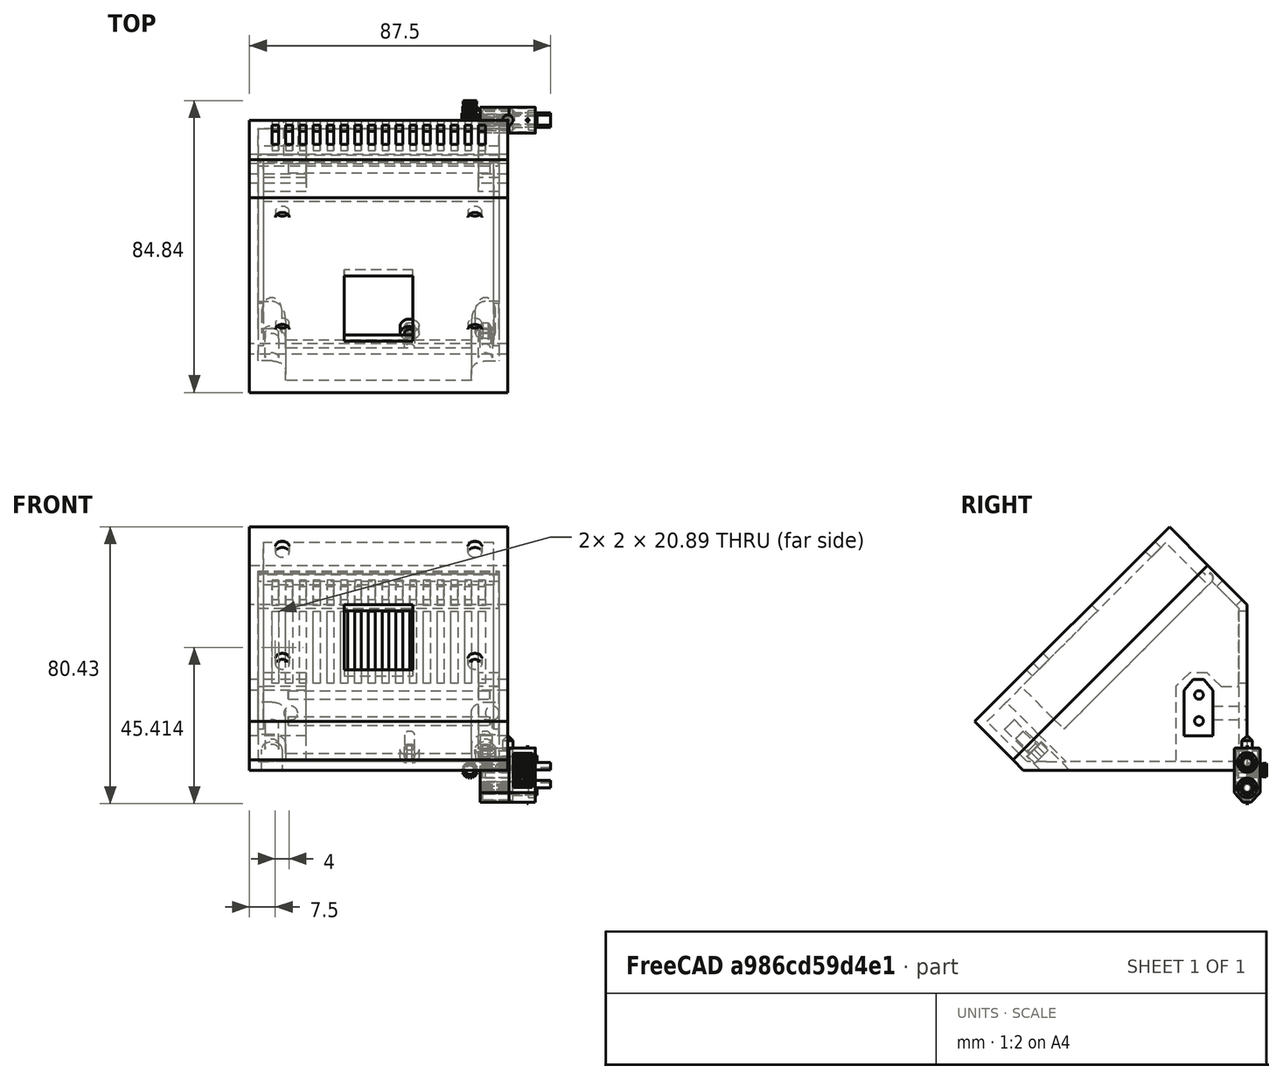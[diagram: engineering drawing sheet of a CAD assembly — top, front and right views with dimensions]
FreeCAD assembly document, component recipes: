
FREECAD ASSEMBLY — COMPONENT RECIPES ("moduleLidl_002_surBase35mm_009.1")

This assembly document has 8 components, labeled P0..P7 below (a component is one placed body or linked part). 4 of them carry a construction recipe — the FreeCAD feature program that regenerates the part from scratch, quoted from this document or its linked companion documents; the rest are supplied as boundary geometry only. No exploded tour is included for this assembly.
COMPONENT P0 — geometry summary ("adapt"; no construction recipe available for this part):
  bounding box: 65.0 x 49.5 x 49.5 mm
  tessellated surface: 2,488 triangles
  volume: 18576 mm^3 (12% of its bounding box)
COMPONENT P1 — geometry summary ("fuse"; no construction recipe available for this part):
  bounding box: 31.7 x 29.8 x 15.0 mm
  tessellated surface: 6,264 triangles
  volume: 2885 mm^3 (20% of its bounding box)
  symmetry: mirror-symmetric across its x mid-plane
COMPONENT P2 — recipe-attached ("tigeLaiton001", modeled in this document).
Construction recipe (the document's own serialized feature program — sketch geometry with constraints, then the solid features built on it; lengths are millimeters unless a unit is written):

FEATURE [PartDesign::Plane] DatumPlane012  label="planBaseTige"
  AttachmentOffset = pos=(0,0,-5.18) rot=(0,0,1;0rad)
  Length = 60
  MapMode = 5
  Placement = pos=(-5.18,1.2e-15,-1.2e-15) rot=(0.57735,0.57735,0.57735;2.0944rad)
  ResizeMode = 0
  Support = -> [YZ_Plane012]
  Width = 60
  expr: .AttachmentOffset.Base.z = -<<tige>>.planBaseTigeposX
FEATURE [Sketcher::SketchObject] Sketch032  label="sk_tiges"
  FullyConstrained = true
  MapMode = 5
  Placement = pos=(-5.18,1.2e-15,-1.2e-15) rot=(0.57735,0.57735,0.57735;2.0944rad)
  Support = -> [DatumPlane012]
  expr: Constraints[0] = <<tige>>.tigeDiam
  expr: Constraints[1] = <<tige>>.tigePosY
  expr: Constraints[2] = <<tige>>.tigePosX
  sketch-geometry (1):
    g0: Circle CenterX=-14 CenterY=14.3 CenterZ=0 NormalX=0 NormalY=0 NormalZ=1 AngleXU=0 Radius=1.25
  constraints (3):
    c: Diameter(g0) = 2.5
    c: DistanceY(g-1,g0) = 14.3
    c: DistanceX(g0,g-1) = 14
FEATURE [PartDesign::Pad] Pad017  label="tigeBasse"
  AllowMultiFace = false
  Direction = (1,-1e-16,1e-16)
  Length = 58.62
  Length2 = 100
  Placement = pos=(-5.18,1e-15,-1e-15) rot=(0.57735,0.57735,0.57735;2.0944rad)
  Profile = -> Sketch032
  Reversed = true
  Type = 0
  expr: Length = <<tige>>.tigeLong
FEATURE [PartDesign::Body] Body007  label="tigeLaiton"
  Group = -> [DatumPlane012,Sketch032,Pad017]
  Origin = -> Origin016
  Tip = -> Pad017
FEATURE [PartDesign::Plane] DatumPlane013  label="planTige2"
  AttachmentOffset = pos=(0,0,-5.18) rot=(0,0,1;0rad)
  Length = 60
  MapMode = 5
  Placement = pos=(-5.18,1.2e-15,-1.2e-15) rot=(0.57735,0.57735,0.57735;2.0944rad)
  ResizeMode = 0
  Support = -> [YZ_Plane014]
  Width = 60
  expr: .AttachmentOffset.Base.z = -<<tige>>.planBaseTigeposX
FEATURE [Sketcher::SketchObject] Sketch033  label="sk_tige2"
  FullyConstrained = true
  MapMode = 5
  Placement = pos=(-5.18,1.2e-15,-1.2e-15) rot=(0.57735,0.57735,0.57735;2.0944rad)
  Support = -> [DatumPlane013]
  expr: Constraints[0] = <<tige>>.tigeDiam
  expr: Constraints[1] = <<tige>>.tigePosX
  expr: Constraints[2] = <<tige>>.tigePosY + <<tige>>.xtEcartBroches
  sketch-geometry (1):
    g0: Circle CenterX=-14 CenterY=21.86 CenterZ=0 NormalX=0 NormalY=0 NormalZ=1 AngleXU=0 Radius=1.25
  constraints (3):
    c: Diameter(g0) = 2.5
    c: DistanceX(g0,g-1) = 14
    c: DistanceY(g-1,g0) = 21.86
FEATURE [PartDesign::Pad] Pad018
  AllowMultiFace = false
  Direction = (1,-1e-16,1e-16)
  Length = 58.62
  Length2 = 100
  Placement = pos=(-5.18,1e-15,-1e-15) rot=(0.57735,0.57735,0.57735;2.0944rad)
  Profile = -> Sketch033
  Reversed = true
  Type = 0
  expr: Length = <<tige>>.tigeLong
FEATURE [PartDesign::Body] Body008  label="tige2"
  Group = -> [DatumPlane013,Sketch033,Pad018]
  Origin = -> Origin018
  Tip = -> Pad018
COMPONENT P3 — geometry summary ("xtVisInsertFix"; no construction recipe available for this part):
  bounding box: 20.2 x 17.7 x 16.6 mm
  tessellated surface: 21,322 triangles
  volume: 1306 mm^3 (22% of its bounding box)
COMPONENT P4 — recipe-attached ("visInsertFavFix", modeled in this document).
Construction recipe (the document's own serialized feature program — sketch geometry with constraints, then the solid features built on it; lengths are millimeters unless a unit is written):

FEATURE [Sketcher::SketchObject] Sketch034  label="Sketch"
  FullyConstrained = false
  MapMode = 5
  Support = -> [XY_Plane015]
  sketch-geometry (1):
    g0: Circle CenterX=0 CenterY=0 CenterZ=0 NormalX=0 NormalY=0 NormalZ=1 AngleXU=0 Radius=2.75
  constraints (2):
    c: Coincident(g0,g-1)
    c: Diameter(g0) = 5.5
FEATURE [PartDesign::Pad] Pad019  label="tete"
  AllowMultiFace = false
  Direction = (1,1,1)
  Length = 3
  Length2 = 100
  Profile = -> Sketch034
  Type = 0
FEATURE [Sketcher::SketchObject] Sketch001
  FullyConstrained = false
  MapMode = 5
  Placement = pos=(0,0,0) rot=(1,0,0;3.14159rad)
  Support = -> [Pad019]
  sketch-geometry (1):
    g0: Circle CenterX=0 CenterY=0 CenterZ=0 NormalX=0 NormalY=0 NormalZ=1 AngleXU=0 Radius=1.5
  constraints (2):
    c: Coincident(g0,g-1)
    c: Diameter(g0) = 3
FEATURE [PartDesign::Pad] Pad020  label="corps"
  AllowMultiFace = false
  BaseFeature = -> Pad019
  Direction = (1,1,1)
  Length = 6
  Length2 = 100
  Profile = -> Sketch001
  Type = 0
FEATURE [PartDesign::Plane] DatumPlane014
  AttachmentOffset = pos=(0,0,3) rot=(0,0,1;0rad)
  Length = 60
  MapMode = 5
  Placement = pos=(0,0,3) rot=(0,0,1;0rad)
  ResizeMode = 0
  Support = -> [XY_Plane015]
  Width = 60
FEATURE [Sketcher::SketchObject] Sketch035  label="Sketch002"
  FullyConstrained = false
  MapMode = 5
  Placement = pos=(0,0,3) rot=(0,0,1;0rad)
  Support = -> [DatumPlane014]
  sketch-geometry (7):
    g0: LineSegment StartX=0.721688 StartY=-1.25 StartZ=0 EndX=1.44338 EndY=1.0119e-12 EndZ=0
    g1: LineSegment StartX=1.44338 StartY=1.0119e-12 StartZ=0 EndX=0.721688 EndY=1.25 EndZ=0
    g2: LineSegment StartX=0.721688 StartY=1.25 StartZ=0 EndX=-0.721688 EndY=1.25 EndZ=0
    g3: LineSegment StartX=-0.721688 StartY=1.25 StartZ=0 EndX=-1.44338 EndY=8.689e-13 EndZ=0
    g4: LineSegment StartX=-1.44338 StartY=8.689e-13 StartZ=0 EndX=-0.721688 EndY=-1.25 EndZ=0
    g5: LineSegment StartX=-0.721688 StartY=-1.25 StartZ=0 EndX=0.721688 EndY=-1.25 EndZ=0
    g6: Circle CenterX=0 CenterY=0 CenterZ=0 NormalX=0 NormalY=0 NormalZ=1 AngleXU=0 Radius=1.44338
  constraints (16):
    c: Coincident(g0,g1)
    c: Coincident(g1,g2)
    c: Coincident(g2,g3)
    c: Coincident(g3,g4)
    c: Coincident(g4,g5)
    c: Coincident(g5,g0)
    c: Equal(g0, g1-g5) x5
    c: PointOnObject(g0,g6)
    c: PointOnObject(g1,g6)
    c: PointOnObject(g2,g6)
    c: PointOnObject(g3,g6)
    c: PointOnObject(g4,g6)
    c: PointOnObject(g5,g6)
    c: Coincident(g6,g-1)
    c: Horizontal(g2)
    c: DistanceY(g0,g1) = 2.5
FEATURE [PartDesign::Pocket] Pocket016  label="emprunte"
  AllowMultiFace = false
  BaseFeature = -> Pad020
  Direction = (1,1,1)
  Length = 4
  Length2 = 100
  Profile = -> Sketch035
  Type = 0
FEATURE [PartDesign::Body] Body009  label="visTHCM3x6_FAV001"
  Group = -> [Sketch034,Pad019,Sketch001,Pad020,DatumPlane014,Sketch035,Pocket016]
  Origin = -> Origin019
  Placement = pos=(-6.5,-61.8718,6.01041) rot=(1,0,0;3.92699rad)
  Tip = -> Pocket016
COMPONENT P5 — recipe-attached ("visInserFavMob", modeled in this document).
Construction recipe (the document's own serialized feature program — sketch geometry with constraints, then the solid features built on it; lengths are millimeters unless a unit is written):

FEATURE [Sketcher::SketchObject] Sketch036
  FullyConstrained = false
  MapMode = 5
  Support = -> [XY_Plane016]
  sketch-geometry (1):
    g0: Circle CenterX=0 CenterY=0 CenterZ=0 NormalX=0 NormalY=0 NormalZ=1 AngleXU=0 Radius=2.75
  constraints (2):
    c: Coincident(g0,g-1)
    c: Diameter(g0) = 5.5
FEATURE [PartDesign::Pad] Pad021  label="tete001"
  AllowMultiFace = false
  Direction = (1,1,1)
  Length = 3
  Length2 = 100
  Profile = -> Sketch036
  Type = 0
FEATURE [Sketcher::SketchObject] Sketch037
  FullyConstrained = false
  MapMode = 5
  Placement = pos=(0,0,0) rot=(1,0,0;3.14159rad)
  Support = -> [Pad021]
  sketch-geometry (1):
    g0: Circle CenterX=0 CenterY=0 CenterZ=0 NormalX=0 NormalY=0 NormalZ=1 AngleXU=0 Radius=1.5
  constraints (2):
    c: Coincident(g0,g-1)
    c: Diameter(g0) = 3
FEATURE [PartDesign::Pad] Pad022  label="corps001"
  AllowMultiFace = false
  BaseFeature = -> Pad021
  Direction = (1,1,1)
  Length = 6
  Length2 = 100
  Profile = -> Sketch037
  Type = 0
FEATURE [PartDesign::Plane] DatumPlane015
  AttachmentOffset = pos=(0,0,3) rot=(0,0,1;0rad)
  Length = 60
  MapMode = 5
  Placement = pos=(0,0,3) rot=(0,0,1;0rad)
  ResizeMode = 0
  Support = -> [XY_Plane016]
  Width = 60
FEATURE [Sketcher::SketchObject] Sketch038
  FullyConstrained = false
  MapMode = 5
  Placement = pos=(0,0,3) rot=(0,0,1;0rad)
  Support = -> [DatumPlane015]
  sketch-geometry (7):
    g0: LineSegment StartX=0.721688 StartY=-1.25 StartZ=0 EndX=1.44338 EndY=1.0119e-12 EndZ=0
    g1: LineSegment StartX=1.44338 StartY=1.0119e-12 StartZ=0 EndX=0.721688 EndY=1.25 EndZ=0
    g2: LineSegment StartX=0.721688 StartY=1.25 StartZ=0 EndX=-0.721688 EndY=1.25 EndZ=0
    g3: LineSegment StartX=-0.721688 StartY=1.25 StartZ=0 EndX=-1.44338 EndY=8.689e-13 EndZ=0
    g4: LineSegment StartX=-1.44338 StartY=8.689e-13 StartZ=0 EndX=-0.721688 EndY=-1.25 EndZ=0
    g5: LineSegment StartX=-0.721688 StartY=-1.25 StartZ=0 EndX=0.721688 EndY=-1.25 EndZ=0
    g6: Circle CenterX=0 CenterY=0 CenterZ=0 NormalX=0 NormalY=0 NormalZ=1 AngleXU=0 Radius=1.44338
  constraints (16):
    c: Coincident(g0,g1)
    c: Coincident(g1,g2)
    c: Coincident(g2,g3)
    c: Coincident(g3,g4)
    c: Coincident(g4,g5)
    c: Coincident(g5,g0)
    c: Equal(g0, g1-g5) x5
    c: PointOnObject(g0,g6)
    c: PointOnObject(g1,g6)
    c: PointOnObject(g2,g6)
    c: PointOnObject(g3,g6)
    c: PointOnObject(g4,g6)
    c: PointOnObject(g5,g6)
    c: Coincident(g6,g-1)
    c: Horizontal(g2)
    c: DistanceY(g0,g1) = 2.5
FEATURE [PartDesign::Pocket] Pocket017  label="emprunte001"
  AllowMultiFace = false
  BaseFeature = -> Pad022
  Direction = (1,1,1)
  Length = 4
  Length2 = 100
  Profile = -> Sketch038
  Type = 0
FEATURE [PartDesign::Body] Body010  label="visTHCM3x6_FAV002"
  Group = -> [Sketch036,Pad021,Sketch037,Pad022,DatumPlane015,Sketch038,Pocket017]
  Origin = -> Origin020
  Placement = pos=(-28.5,-61.8718,6.01041) rot=(1,0,0;3.92699rad)
  Tip = -> Pocket017
COMPONENT P6 — recipe-attached ("BaseModule", modeled in this document).
Construction recipe (the document's own serialized feature program — sketch geometry with constraints, then the solid features built on it; lengths are millimeters unless a unit is written):

FEATURE [PartDesign::FeatureBase] Clone
  BaseFeature = -> Slice_child0
FEATURE [PartDesign::FeatureBase] Clone001
  BaseFeature = -> Slice_child1
FEATURE [PartDesign::Thickness] Thickness
  Base = -> Clone [Face7]
  BaseFeature = -> Clone
  Intersection = false
  Join = 0
  Mode = 0
  Reversed = true
  SupportTransform = false
  Value = 2.5
  expr: Value = <<sp>>.epaisseurParois
FEATURE [PartDesign::Thickness] Thickness001
  Base = -> Clone001 [Face5]
  BaseFeature = -> Clone001
  Intersection = false
  Join = 0
  Mode = 0
  Reversed = true
  SupportTransform = false
  Value = 2.5
  expr: Value = <<sp>>.epaisseurParois
FEATURE [PartDesign::Plane] DatumPlane001  label="planXt"
  AttachmentOffset = pos=(0,0,-2.5) rot=(0,0,1;0rad)
  Length = 110.737
  MapMode = 5
  Placement = pos=(-2.5,6e-16,-6e-16) rot=(0.57735,0.57735,0.57735;2.0944rad)
  ResizeMode = 0
  Support = -> [YZ_Plane002]
  Width = 102.305
  expr: .AttachmentOffset.Base.z = -<<sp>>.epaisseurParois
FEATURE [Sketcher::SketchObject] Sketch002  label="sk_renfortXt"
  FullyConstrained = true
  MapMode = 5
  Placement = pos=(-2.5,6e-16,-6e-16) rot=(0.57735,0.57735,0.57735;2.0944rad)
  Support = -> [DatumPlane001]
  expr: .Constraints.dist = <<sp>>.xt60distanceAngleBord
  expr: .Constraints.epRf = <<sp>>.xt60epRenfort
  expr: Constraints[13] = <<sp>>.xt60largeurFetiere
  expr: Constraints[14] = <<sp>>.xt60hauteur
  expr: Constraints[15] = <<sp>>.xt60hauteurToit
  expr: Constraints[16] = <<sp>>.xt60base
  expr: Constraints[18] = .Constraints.dist
  expr: Constraints[31] = <<sp>>.epaisseurParois
  expr: Constraints[32] = .Constraints.epRf
  expr: Constraints[34] = .Constraints.epRf
  expr: Constraints[45] = <<sp>>.epaisseurParois
  sketch-geometry (17):
    g0: LineSegment StartX=-18.3 StartY=10 StartZ=0 EndX=-18.3 EndY=23.25 EndZ=0
    g1: LineSegment StartX=-18.3 StartY=23.25 StartZ=0 EndX=-15.65 EndY=25.75 EndZ=0
    g2: LineSegment StartX=-15.65 StartY=25.75 StartZ=0 EndX=-12.65 EndY=25.75 EndZ=0
    g3: LineSegment StartX=-12.65 StartY=25.75 StartZ=0 EndX=-10 EndY=23.25 EndZ=0
    g4: LineSegment StartX=-10 StartY=23.25 StartZ=0 EndX=-10 EndY=10 EndZ=0
    g5: LineSegment StartX=-10 StartY=10 StartZ=0 EndX=-18.3 EndY=10 EndZ=0
    g6: LineSegment StartX=-14.15 StartY=10 StartZ=0 EndX=-14.15 EndY=25.75 EndZ=0
    g7: LineSegment StartX=-16.6431 StartY=28.25 StartZ=0 EndX=-20.8 EndY=24.3284 EndZ=0
    g8: LineSegment StartX=-20.8 StartY=24.3284 StartZ=0 EndX=-20.8 EndY=2.5 EndZ=0
    g9: LineSegment StartX=-20.8 StartY=2.5 StartZ=0 EndX=-7.5 EndY=2.5 EndZ=0
    g10: LineSegment StartX=-7.5 StartY=2.5 StartZ=0 EndX=-7.5 EndY=24.3284 EndZ=0
    g11: LineSegment StartX=-7.5 StartY=24.3284 StartZ=0 EndX=-11.6569 EndY=28.25 EndZ=0
    g12: LineSegment StartX=-11.6569 StartY=28.25 StartZ=0 EndX=-16.6431 EndY=28.25 EndZ=0
    g13: LineSegment StartX=-7.5 StartY=24.3284 StartZ=0 EndX=-2.5 EndY=24.3284 EndZ=0
    g14: LineSegment StartX=-2.5 StartY=24.3284 StartZ=0 EndX=-2.5 EndY=2.5 EndZ=0
    g15: LineSegment StartX=-2.5 StartY=2.5 StartZ=0 EndX=-7.5 EndY=2.5 EndZ=0
    g16: LineSegment StartX=-7.5 StartY=2.5 StartZ=0 EndX=-7.5 EndY=24.3284 EndZ=0
  constraints (46):
    c: Vertical(g0)
    c: Coincident(g0,g1)
    c: Coincident(g1,g2)
    c: Horizontal(g2)
    c: Coincident(g2,g3)
    c: Coincident(g3,g4)
    c: Vertical(g4)
    c: Coincident(g4,g5)
    c: Coincident(g5,g0)
    c: Horizontal(g5)
    c: Symmetric(g1,g2,g6)
    c: Equal(g0,g4)
    c: Symmetric(g0,g4,g6)
    c: DistanceX(g2,g2) = 3
    c: DistanceY(g4,g4) = 13.25
    c: DistanceY(g3,g2) = 2.5
    c: DistanceX(g5,g5) = 8.3
    c: DistanceX(g4,g-1) = 10  'dist'
    c: DistanceY(g-1,g4) = 10
    c: Coincident(g7,g8)
    c: Vertical(g8)
    c: Coincident(g8,g9)
    c: Horizontal(g9)
    c: Coincident(g9,g10)
    c: Coincident(g10,g11)
    c: Coincident(g11,g12)
    c: Coincident(g12,g7)
    c: Symmetric(g7,g10,g6)
    c: Symmetric(g7,g11,g6)
    c: Symmetric(g8,g9,g6)
    c: DistanceX(g8,g0) = 2.5  'epRf'
    c: DistanceY(g-1,g9) = 2.5
    c: Distance(g7,g1) = 2.5
    c: Parallel(g1,g7)
    c: DistanceY(g2,g11) = 2.5
    c: Coincident(g13,g14)
    c: Coincident(g14,g15)
    c: Coincident(g15,g16)
    c: Coincident(g16,g13)
    c: Horizontal(g13)
    c: Horizontal(g15)
    c: Vertical(g14)
    c: Vertical(g16)
    c: Coincident(g13,g11)
    c: Horizontal(g14,g9)
    c: DistanceX(g14,g-1) = 2.5
FEATURE [PartDesign::Pad] Pad001  label="renfortXt"
  AllowMultiFace = false
  BaseFeature = -> Thickness
  Direction = (1,-1e-16,1e-16)
  Length = 70
  Length2 = 100
  Profile = -> Sketch002
  Reversed = true
  Type = 0
  expr: Length = <<sp>>.largeurModuleBase - 2 * <<sp>>.epaisseurParois
FEATURE [Sketcher::SketchObject] Sketch003  label="sk_trouXt"
  FullyConstrained = true
  MapMode = 5
  Placement = pos=(0,0,0) rot=(0.57735,0.57735,0.57735;2.0944rad)
  Support = -> [YZ_Plane002]
  expr: .Constraints.dist = <<sp>>.xt60distanceAngleBord
  expr: Constraints[13] = <<sp>>.xt60base
  expr: Constraints[14] = <<sp>>.xt60hauteur
  expr: Constraints[15] = <<sp>>.xt60hauteurToit + <<sp>>.xtJeu
  expr: Constraints[16] = <<sp>>.xt60largeurFetiere
  expr: Constraints[18] = .Constraints.dist
  sketch-geometry (7):
    g0: LineSegment StartX=-18.3 StartY=10 StartZ=0 EndX=-18.3 EndY=23.25 EndZ=0
    g1: LineSegment StartX=-18.3 StartY=23.25 StartZ=0 EndX=-15.65 EndY=26.35 EndZ=0
    g2: LineSegment StartX=-15.65 StartY=26.35 StartZ=0 EndX=-12.65 EndY=26.35 EndZ=0
    g3: LineSegment StartX=-12.65 StartY=26.35 StartZ=0 EndX=-10 EndY=23.25 EndZ=0
    g4: LineSegment StartX=-10 StartY=23.25 StartZ=0 EndX=-10 EndY=10 EndZ=0
    g5: LineSegment StartX=-10 StartY=10 StartZ=0 EndX=-18.3 EndY=10 EndZ=0
    g6: LineSegment StartX=-14.15 StartY=10 StartZ=0 EndX=-14.15 EndY=26.35 EndZ=0
  constraints (19):
    c: Vertical(g0)
    c: Coincident(g0,g1)
    c: Coincident(g1,g2)
    c: Horizontal(g2)
    c: Coincident(g2,g3)
    c: Coincident(g3,g4)
    c: Coincident(g4,g5)
    c: Coincident(g5,g0)
    c: Horizontal(g5)
    c: Symmetric(g1,g2,g6)
    c: Symmetric(g0,g3,g6)
    c: Vertical(g6)
    c: Symmetric(g0,g4,g6)
    c: DistanceX(g5,g5) = 8.3
    c: DistanceY(g4,g4) = 13.25
    c: DistanceY(g3,g2) = 3.1
    c: DistanceX(g2,g2) = 3
    c: DistanceX(g4,g-1) = 10  'dist'
    c: DistanceY(g-1,g4) = 10
FEATURE [PartDesign::Pocket] Pocket
  AllowMultiFace = false
  BaseFeature = -> Pad001
  Direction = (-1,2e-16,-3e-16)
  Length = 75
  Length2 = 100
  Profile = -> Sketch003
  Type = 0
  expr: Length = <<sp>>.largeurModuleBase
FEATURE [PartDesign::Plane] DatumPlane002  label="planDecoupeRenfortXt"
  AttachmentOffset = pos=(0,0,2.5) rot=(0,0,1;0rad)
  Length = 118.392
  MapMode = 5
  Placement = pos=(0,-2.5,-6e-16) rot=(1,0,0;1.5708rad)
  ResizeMode = 0
  Support = -> [XZ_Plane002]
  Width = 102.961
  expr: .AttachmentOffset.Base.z = <<sp>>.epaisseurParois
FEATURE [Sketcher::SketchObject] Sketch004  label="sk_decoupRenfXt"
  FullyConstrained = true
  MapMode = 5
  Placement = pos=(0,-2.5,-6e-16) rot=(1,0,0;1.5708rad)
  Support = -> [DatumPlane002]
  expr: Constraints[10] = <<sp>>.xt60LongueurRenfortPetit + <<sp>>.epaisseurParois
  expr: Constraints[11] = <<sp>>.largeurModuleBase - (<<sp>>.xt60longueurRenfortGrand + <<sp>>.epaisseurParois)
  expr: Constraints[8] = <<sp>>.epaisseurParois
  expr: Constraints[9] = <<sp>>.xt60distanceAngleBord + <<sp>>.xt60hauteur + <<sp>>.xt60hauteurToit + <<sp>>.xt60epRenfort
  sketch-geometry (4):
    g0: LineSegment StartX=-58.5 StartY=28.25 StartZ=0 EndX=-8.5 EndY=28.25 EndZ=0
    g1: LineSegment StartX=-8.5 StartY=28.25 StartZ=0 EndX=-8.5 EndY=2.5 EndZ=0
    g2: LineSegment StartX=-8.5 StartY=2.5 StartZ=0 EndX=-58.5 EndY=2.5 EndZ=0
    g3: LineSegment StartX=-58.5 StartY=2.5 StartZ=0 EndX=-58.5 EndY=28.25 EndZ=0
  constraints (12):
    c: Coincident(g0,g1)
    c: Coincident(g1,g2)
    c: Coincident(g2,g3)
    c: Coincident(g3,g0)
    c: Horizontal(g0)
    c: Horizontal(g2)
    c: Vertical(g1)
    c: Vertical(g3)
    c: DistanceY(g-1,g1) = 2.5
    c: DistanceY(g-1,g0) = 28.25
    c: DistanceX(g1,g-1) = 8.5
    c: DistanceX(g2,g-1) = 58.5
FEATURE [PartDesign::Pocket] Pocket001  label="decoupeRenfXt"
  AllowMultiFace = false
  BaseFeature = -> Pocket
  Direction = (0,1,2e-16)
  Length = 23.3
  Length2 = 100
  Profile = -> Sketch004
  Reversed = true
  Type = 0
  expr: Length = <<sp>>.xt60distanceAngleBord + <<sp>>.xt60base + 2 * <<sp>>.xt60epRenfort
FEATURE [Sketcher::SketchObject] Sketch005  label="xt60PercagePostMale"
  FullyConstrained = true
  MapMode = 5
  Placement = pos=(0,0,0) rot=(1,0,0;1.5708rad)
  Support = -> [XZ_Plane002]
  expr: Constraints[0] = <<sp>>.insertDiamPercage
  expr: Constraints[1] = <<sp>>.insertDistanceTrouBordMale
  expr: Constraints[2] = <<sp>>.insertHauteur
  sketch-geometry (1):
    g0: Circle CenterX=-4.5 CenterY=16.625 CenterZ=0 NormalX=0 NormalY=0 NormalZ=1 AngleXU=0 Radius=2
  constraints (3):
    c: Diameter(g0) = 4
    c: DistanceX(g0,g-1) = 4.5
    c: DistanceY(g-1,g0) = 16.625
FEATURE [PartDesign::Pocket] Pocket002  label="insertXtMale"
  AllowMultiFace = false
  BaseFeature = -> Pocket001
  Direction = (0,1,2e-16)
  Length = 10
  Length2 = 100
  Profile = -> Sketch005
  Reversed = true
  Type = 0
  expr: Length = <<sp>>.insertProfondeurPercage
FEATURE [Sketcher::SketchObject] Sketch006  label="xt60PercagePostFem"
  FullyConstrained = true
  MapMode = 5
  Placement = pos=(0,0,0) rot=(1,0,0;1.5708rad)
  Support = -> [XZ_Plane002]
  expr: Constraints[0] = <<sp>>.insertDiamPercage
  expr: Constraints[1] = <<sp>>.insertDistanceTrouBordFem
  expr: Constraints[2] = <<sp>>.insertHauteur
  sketch-geometry (1):
    g0: Circle CenterX=-63 CenterY=16.625 CenterZ=0 NormalX=0 NormalY=0 NormalZ=1 AngleXU=0 Radius=2
  constraints (3):
    c: Diameter(g0) = 4
    c: DistanceX(g0,g-1) = 63
    c: DistanceY(g-1,g0) = 16.625
FEATURE [PartDesign::Pocket] Pocket003  label="insertXt60Fem"
  AllowMultiFace = false
  BaseFeature = -> Pocket002
  Direction = (0,1,2e-16)
  Length = 10
  Length2 = 100
  Profile = -> Sketch006
  Reversed = true
  Type = 0
  expr: Length = <<sp>>.insertProfondeurPercage
FEATURE [PartDesign::Plane] DatumPlane003
  AttachmentOffset = pos=(0,0,2.5) rot=(0,0,1;0rad)
  Length = 119.287
  MapMode = 2
  Placement = pos=(0,0,2.5) rot=(0,0,1;0rad)
  ResizeMode = 0
  Support = -> [XY_Plane002]
  Width = 112.287
  expr: .AttachmentOffset.Base.z = <<sp>>.epaisseurParois
FEATURE [PartDesign::Plane] DatumPlane004  label="planTrancheur"
  AttachmentOffset = pos=(0,0,71) rot=(-1,0,0;0.785398rad)
  Length = 122.411
  MapMode = 5
  Placement = pos=(0,-71,-1.58e-14) rot=(1,0,0;0.785398rad)
  ResizeMode = 0
  Support = -> [XZ_Plane002]
  Width = 147.971
  expr: .AttachmentOffset.Base.z = <<sp>>.planTrancheur
FEATURE [Sketcher::SketchObject] Sketch008
  FullyConstrained = true
  MapMode = 5
  Placement = pos=(0,-71,-2.13e-14) rot=(1,0,0;0.785398rad)
  Support = -> [DatumPlane004]
  expr: .Constraints.dist = <<sp>>.epaisseurParois
  expr: Constraints[13] = <<sp>>.epaisseurParois
  expr: Constraints[16] = <<sp>>.insertDiamPercage / 2 + <<sp>>.insertFAVMargeDist
  expr: Constraints[1] = <<sp>>.insertFavDistAuZeroDuPLan
  expr: Constraints[21] = <<sp>>.insertFAVDistBord
  expr: Constraints[22] = <<sp>>.largeurModuleBase - <<sp>>.epaisseurParois
  sketch-geometry (7):
    g0: LineSegment StartX=-2.5 StartY=4.24264 StartZ=0 EndX=-72.5 EndY=4.24264 EndZ=0
    g1: LineSegment StartX=-6.5 StartY=14.7426 StartZ=0 EndX=-2.5 EndY=14.7426 EndZ=0
    g2: LineSegment StartX=-2.5 StartY=14.7426 StartZ=0 EndX=-2.5 EndY=6.74264 EndZ=0
    g3: LineSegment StartX=-2.5 StartY=6.74264 StartZ=0 EndX=-10.5 EndY=6.74264 EndZ=0
    g4: LineSegment StartX=-10.5 StartY=6.74264 StartZ=0 EndX=-10.5 EndY=10.7426 EndZ=0
    g5: ArcOfCircle CenterX=-6.5 CenterY=10.7426 CenterZ=0 NormalX=0 NormalY=0 NormalZ=1 AngleXU=0 Radius=4 StartAngle=1.5708 EndAngle=3.14159
    g6: LineSegment StartX=-6.5 StartY=10.7426 StartZ=0 EndX=-6.5 EndY=6.74264 EndZ=0
  constraints (23):
    c: Horizontal(g0)
    c: DistanceY(g-1,g0) = 4.24264
    c: DistanceX(g0,g-1) = 2.5  'dist'
    c: Horizontal(g1)
    c: Coincident(g1,g2)
    c: Vertical(g2)
    c: Coincident(g2,g3)
    c: Horizontal(g3)
    c: Coincident(g3,g4)
    c: Vertical(g4)
    c: Vertical(g2,g0)
    c: Equal(g3,g2)
    c: Equal(g4,g1)
    c: DistanceY(g0,g2) = 2.5
    c: Coincident(g5,g4)
    c: Coincident(g5,g1)
    c: DistanceX(g5,g2) = 4
    c: Coincident(g6,g5)
    c: PointOnObject(g6,g3)
    c: Vertical(g6)
    c: Vertical(g5,g1)
    c: DistanceX(g3,g3) = 8
    c: DistanceX(g0,g-1) = 72.5
FEATURE [PartDesign::Pad] Pad003  label="padTrouFAVDroite"
  AllowMultiFace = false
  BaseFeature = -> Pocket003
  Direction = (0,-0.707107,0.707107)
  Length = 10
  Length2 = 100
  Profile = -> Sketch008
  Reversed = true
  Type = 3
  UpToFace = -> DatumPlane003
FEATURE [Sketcher::SketchObject] Sketch009
  FullyConstrained = true
  MapMode = 5
  Placement = pos=(0,-71,-2.13e-14) rot=(1,0,0;0.785398rad)
  Support = -> [DatumPlane004]
  expr: .Constraints.larg = <<sp>>.insertFAVDistBord
  expr: Constraints[11] = .Constraints.larg / 2
  expr: Constraints[12] = <<sp>>.largeurModuleBase
  expr: Constraints[13] = <<sp>>.insertFavDistAuZeroDuPLan
  expr: Constraints[14] = <<sp>>.epaisseurParois
  expr: Constraints[15] = <<sp>>.epaisseurParois
  expr: Constraints[8] = .Constraints.larg
  sketch-geometry (6):
    g0: LineSegment StartX=-72.5 StartY=6.74264 StartZ=0 EndX=-64.5 EndY=6.74264 EndZ=0
    g1: LineSegment StartX=-64.5 StartY=6.74264 StartZ=0 EndX=-64.5 EndY=10.7426 EndZ=0
    g2: LineSegment StartX=-68.5 StartY=14.7426 StartZ=0 EndX=-72.5 EndY=14.7426 EndZ=0
    g3: LineSegment StartX=-72.5 StartY=14.7426 StartZ=0 EndX=-72.5 EndY=6.74264 EndZ=0
    g4: ArcOfCircle CenterX=-68.5 CenterY=10.7426 CenterZ=0 NormalX=0 NormalY=0 NormalZ=1 AngleXU=0 Radius=4 StartAngle=0 EndAngle=1.5708
    g5: GeomPoint X=-75 Y=4.24264 Z=0
  constraints (16):
    c: Coincident(g0,g1)
    c: Coincident(g2,g3)
    c: Coincident(g3,g0)
    c: Horizontal(g0)
    c: Horizontal(g2)
    c: Vertical(g1)
    c: Vertical(g3)
    c: DistanceX(g0,g0) = 8  'larg'
    c: DistanceY(g3,g3) = 8
    c: Tangent(g2,g4) = -1.5708
    c: Tangent(g1,g4) = -1.5708
    c: DistanceX(g0,g4) = 4
    c: DistanceX(g5,g-1) = 75
    c: DistanceY(g-1,g5) = 4.24264
    c: DistanceX(g5,g0) = 2.5
    c: DistanceY(g5,g0) = 2.5
FEATURE [PartDesign::Pad] Pad004  label="padTrouFavGauche"
  AllowMultiFace = false
  BaseFeature = -> Pad003
  Direction = (0,-0.707107,0.707107)
  Length = 10
  Length2 = 100
  Profile = -> Sketch009
  Type = 3
  UpToFace = -> DatumPlane003 [Plane]
FEATURE [Sketcher::SketchObject] Sketch010
  FullyConstrained = true
  MapMode = 5
  Placement = pos=(0,-71,-2.13e-14) rot=(1,0,0;0.785398rad)
  Support = -> [DatumPlane004]
  expr: Constraints[0] = <<sp>>.insertFAVDistBord / 2 + <<sp>>.epaisseurParois
  expr: Constraints[1] = <<sp>>.insertFavDistAuZeroDuPLan + <<sp>>.epaisseurParois + <<sp>>.insertFAVDistBord / 2
  expr: Constraints[2] = <<sp>>.insertDiamPercage
  sketch-geometry (1):
    g0: Circle CenterX=-6.5 CenterY=10.7426 CenterZ=0 NormalX=0 NormalY=0 NormalZ=1 AngleXU=0 Radius=2
  constraints (3):
    c: DistanceX(g0,g-1) = 6.5
    c: DistanceY(g-1,g0) = 10.7426
    c: Diameter(g0) = 4
FEATURE [PartDesign::Pocket] Pocket004  label="trouDroit"
  AllowMultiFace = false
  BaseFeature = -> Pad004
  Direction = (0,0.707107,-0.707107)
  Length = 5
  Length2 = 100
  Profile = -> Sketch010
  Type = 1
FEATURE [Sketcher::SketchObject] Sketch011
  FullyConstrained = true
  MapMode = 5
  Placement = pos=(0,-71,-2.13e-14) rot=(1,0,0;0.785398rad)
  Support = -> [DatumPlane004]
  expr: Constraints[0] = <<sp>>.insertDiamPercage
  expr: Constraints[1] = <<sp>>.largeurModuleBase - <<sp>>.epaisseurParois - <<sp>>.insertFAVDistBord / 2
  expr: Constraints[2] = <<sp>>.insertFavDistAuZeroDuPLan + <<sp>>.epaisseurParois + <<sp>>.insertFAVDistBord / 2
  sketch-geometry (1):
    g0: Circle CenterX=-68.5 CenterY=10.7426 CenterZ=0 NormalX=0 NormalY=0 NormalZ=1 AngleXU=0 Radius=2
  constraints (3):
    c: Diameter(g0) = 4
    c: DistanceX(g0,g-1) = 68.5
    c: DistanceY(g-1,g0) = 10.7426
FEATURE [PartDesign::Pocket] Pocket005  label="trouGauche"
  AllowMultiFace = false
  BaseFeature = -> Pocket004
  Direction = (0,0.707107,-0.707107)
  Length = 5
  Length2 = 100
  Profile = -> Sketch011
  Type = 1
FEATURE [PartDesign::Plane] DatumPlane005  label="planTeteVisFav"
  AttachmentOffset = pos=(0,0,68) rot=(-1,0,0;0.785398rad)
  Length = 122.411
  MapMode = 5
  Placement = pos=(0,-68,-1.51e-14) rot=(1,0,0;0.785398rad)
  ResizeMode = 0
  Support = -> [XZ_Plane002]
  Width = 147.971
  expr: .AttachmentOffset.Base.z = <<sp>>.planTrancheur - 3
FEATURE [Sketcher::SketchObject] Sketch012
  ExternalGeometry = -> [Pocket005]
  FullyConstrained = true
  MapMode = 5
  Placement = pos=(0,-68,-1.42e-14) rot=(1,0,0;0.785398rad)
  Support = -> [DatumPlane005]
  expr: Constraints[1] = <<sp>>.visM3DiamEncastrement
  sketch-geometry (2):
    g0: Circle CenterX=-6.5 CenterY=8.62132 CenterZ=0 NormalX=0 NormalY=0 NormalZ=1 AngleXU=0 Radius=3
    g1: Circle CenterX=-68.5 CenterY=8.62132 CenterZ=0 NormalX=0 NormalY=0 NormalZ=1 AngleXU=0 Radius=3
  constraints (4):
    c: Equal(g0,g1)
    c: Diameter(g1) = 6
    c: Coincident(g1,g-4)
    c: Coincident(g-3,g0)
FEATURE [PartDesign::Pocket] Pocket006  label="evidementTeteVisFav"
  AllowMultiFace = false
  BaseFeature = -> Pocket005
  Direction = (0,0.707107,-0.707107)
  Length = 20
  Length2 = 100
  Profile = -> Sketch012
  Type = 1
FEATURE [Sketcher::SketchObject] Sketch014
  FullyConstrained = true
  MapMode = 5
  Placement = pos=(0,0,0) rot=(1,0,0;1.5708rad)
  Support = -> [XZ_Plane002]
  expr: Constraints[12] = <<sp>>.xt60distanceAngleBord + <<sp>>.xt60hauteur + <<sp>>.ventilDistBordFente
  expr: Constraints[13] = <<sp>>.ventilLargeurFentes
  expr: Constraints[14] = <<sp>>.ventilEcartfente / 2
  expr: Constraints[15] = <<sp>>.hauteurDuDos - <<sp>>.ventilDistBordFente
  expr: Constraints[2] = <<sp>>.hauteurDuDos
  expr: Constraints[3] = <<sp>>.largeurModuleBase / 2
  sketch-geometry (5):
    g0: LineSegment StartX=-37.5 StartY=0 StartZ=0 EndX=-37.5 EndY=48.1371 EndZ=0
    g1: LineSegment StartX=-40.5 StartY=46.1371 StartZ=0 EndX=-38.5 EndY=46.1371 EndZ=0
    g2: LineSegment StartX=-38.5 StartY=46.1371 StartZ=0 EndX=-38.5 EndY=25.25 EndZ=0
    g3: LineSegment StartX=-38.5 StartY=25.25 StartZ=0 EndX=-40.5 EndY=25.25 EndZ=0
    g4: LineSegment StartX=-40.5 StartY=25.25 StartZ=0 EndX=-40.5 EndY=46.1371 EndZ=0
  constraints (16):
    c: PointOnObject(g0,g-1)
    c: Vertical(g0)
    c: DistanceY(g0,g0) = 48.1371
    c: DistanceX(g0,g-1) = 37.5
    c: Coincident(g1,g2)
    c: Coincident(g2,g3)
    c: Coincident(g3,g4)
    c: Coincident(g4,g1)
    c: Horizontal(g1)
    c: Horizontal(g3)
    c: Vertical(g2)
    c: Vertical(g4)
    c: DistanceY(g-1,g2) = 25.25
    c: DistanceX(g1,g1) = 2
    c: DistanceX(g2,g0) = 1
    c: DistanceY(g-1,g1) = 46.1371
FEATURE [PartDesign::Pocket] Pocket008  label="ventilFente1"
  AllowMultiFace = false
  BaseFeature = -> Pocket006
  Direction = (0,1,2e-16)
  Length = 2.5
  Length2 = 100
  Profile = -> Sketch014
  Reversed = true
  Type = 0
  expr: Length = <<sp>>.epaisseurParois
FEATURE [PartDesign::LinearPattern] LinearPattern  label="ventilDosRepeat1"
  BaseFeature = -> Pocket008
  Direction = -> Sketch014 [H_Axis]
  Length = 28
  Occurrences = 8
  Originals = -> [Pocket008]
  Reversed = true
  expr: Length = <<sp>>.ventilLargeurRepet
  expr: Occurrences = <<sp>>.ventilNbrFents
FEATURE [PartDesign::LinearPattern] LinearPattern001  label="ventilDosRepeat2"
  BaseFeature = -> LinearPattern
  Direction = -> Sketch014 [H_Axis]
  Length = 32
  Occurrences = 9
  Originals = -> [Pocket008]
  expr: Length = <<sp>>.ventilLargeurRepet + <<sp>>.ventilEcartfente + <<sp>>.ventilLargeurFentes
  expr: Occurrences = <<sp>>.ventilNbrFents + 1
FEATURE [PartDesign::Plane] DatumPlane006  label="planVentilSup"
  AttachmentOffset = pos=(0,0,-48.1371) rot=(1,0,0;0.785398rad)
  Length = 122.411
  MapMode = 5
  Placement = pos=(0,48.1371,1.07e-14) rot=(1,0,0;2.35619rad)
  ResizeMode = 0
  Support = -> [XZ_Plane002]
  Width = 147.971
  expr: .AttachmentOffset.Base.z = -<<sp>>.hauteurDuDos
FEATURE [Sketcher::SketchObject] Sketch015
  FullyConstrained = true
  MapMode = 5
  Placement = pos=(0,48.1371,1.07e-14) rot=(1,0,0;2.35619rad)
  Support = -> [DatumPlane006]
  expr: Constraints[10] = <<sp>>.ventilLargeurFentes
  expr: Constraints[11] = (<<sp>>.largeurModuleBase + <<sp>>.ventilEcartfente) / 2
  expr: Constraints[8] = <<sp>>.distanceAuZeroPlanBorArriere + <<sp>>.ventilDistBordFente
  expr: Constraints[9] = <<sp>>.longPetitRetSupSansFav - 2 * <<sp>>.ventilDistBordFente - <<sp>>.favBordureProf
  sketch-geometry (4):
    g0: LineSegment StartX=-38.5 StartY=78.0926 StartZ=0 EndX=-40.5 EndY=78.0926 EndZ=0
    g1: LineSegment StartX=-40.5 StartY=78.0926 StartZ=0 EndX=-40.5 EndY=70.0761 EndZ=0
    g2: LineSegment StartX=-40.5 StartY=70.0761 StartZ=0 EndX=-38.5 EndY=70.0761 EndZ=0
    g3: LineSegment StartX=-38.5 StartY=70.0761 StartZ=0 EndX=-38.5 EndY=78.0926 EndZ=0
  constraints (12):
    c: Coincident(g0,g1)
    c: Coincident(g1,g2)
    c: Coincident(g2,g3)
    c: Coincident(g3,g0)
    c: Horizontal(g0)
    c: Horizontal(g2)
    c: Vertical(g1)
    c: Vertical(g3)
    c: DistanceY(g-1,g2) = 70.0761
    c: DistanceY(g2,g0) = 8.01652
    c: DistanceX(g0,g0) = 2
    c: DistanceX(g2,g-1) = 38.5
FEATURE [PartDesign::Pocket] Pocket009  label="ventilSupFente"
  AllowMultiFace = false
  BaseFeature = -> LinearPattern001
  Direction = (0,0.707107,0.707107)
  Length = 5
  Length2 = 100
  Profile = -> Sketch015
  Reversed = true
  Type = 0
FEATURE [PartDesign::LinearPattern] LinearPattern002  label="ventilSupRepeat1"
  BaseFeature = -> Pocket009
  Direction = -> Sketch015 [H_Axis]
  Length = 28
  Occurrences = 8
  Originals = -> [Pocket009]
  Reversed = true
  expr: Length = <<sp>>.ventilLargeurRepet
  expr: Occurrences = <<sp>>.ventilNbrFents
FEATURE [PartDesign::LinearPattern] LinearPattern003  label="ventilSupRepeat2"
  BaseFeature = -> LinearPattern002
  Direction = -> Sketch015 [H_Axis]
  Length = 32
  Occurrences = 9
  Originals = -> [Pocket009]
  expr: Length = <<sp>>.ventilLargeurRepet + <<sp>>.ventilEcartfente + <<sp>>.ventilLargeurFentes
  expr: Occurrences = <<sp>>.ventilNbrFents + 1
FEATURE [PartDesign::Plane] DatumPlane007  label="planTrancheurBis"
  AttachmentOffset = pos=(0,0,71) rot=(-1,0,0;0.785398rad)
  Length = 123.775
  MapMode = 5
  Placement = pos=(0,-71,-1.58e-14) rot=(1,0,0;0.785398rad)
  ResizeMode = 0
  Support = -> [XZ_Plane003]
  Width = 165.093
  expr: .AttachmentOffset.Base.z = <<sp>>.planTrancheur
FEATURE [Sketcher::SketchObject] Sketch016  label="sk_insertFavDroit"
  FullyConstrained = true
  MapMode = 5
  Placement = pos=(0,-71,-2.13e-14) rot=(1,0,0;0.785398rad)
  Support = -> [DatumPlane007]
  expr: Constraints[11] = <<sp>>.insertFAVDistBord
  expr: Constraints[14] = <<sp>>.insertFAVDistBord / 2
  expr: Constraints[7] = <<sp>>.epaisseurParois
  expr: Constraints[8] = <<sp>>.insertFavDistAuZeroDuPLan + <<sp>>.epaisseurParois
  expr: Constraints[9] = <<sp>>.insertFAVDistBord
  sketch-geometry (5):
    g0: LineSegment StartX=-6.5 StartY=14.7426 StartZ=0 EndX=-2.5 EndY=14.7426 EndZ=0
    g1: LineSegment StartX=-2.5 StartY=14.7426 StartZ=0 EndX=-2.5 EndY=6.74264 EndZ=0
    g2: LineSegment StartX=-2.5 StartY=6.74264 StartZ=0 EndX=-10.5 EndY=6.74264 EndZ=0
    g3: LineSegment StartX=-10.5 StartY=6.74264 StartZ=0 EndX=-10.5 EndY=10.7426 EndZ=0
    g4: ArcOfCircle CenterX=-6.5 CenterY=10.7426 CenterZ=0 NormalX=0 NormalY=0 NormalZ=1 AngleXU=0 Radius=4 StartAngle=1.5708 EndAngle=3.14159
  constraints (15):
    c: Horizontal(g0)
    c: Coincident(g0,g1)
    c: Vertical(g1)
    c: Coincident(g1,g2)
    c: Horizontal(g2)
    c: Coincident(g2,g3)
    c: Vertical(g3)
    c: DistanceX(g1,g-1) = 2.5
    c: DistanceY(g-1,g1) = 6.74264
    c: DistanceY(g1,g1) = 8
    c: Equal(g3,g0)
    c: DistanceX(g2,g2) = 8
    c: Coincident(g4,g0)
    c: Tangent(g4,g3) = 1.5708
    c: DistanceX(g4,g1) = 4
FEATURE [PartDesign::Pad] Pad005  label="padInsertFavDroit"
  AllowMultiFace = false
  BaseFeature = -> Thickness001
  Direction = (0,-0.707107,0.707107)
  Length = 10
  Length2 = 100
  Profile = -> Sketch016
  Type = 2
FEATURE [Sketcher::SketchObject] Sketch017  label="sp_padInserFavGauch"
  FullyConstrained = true
  MapMode = 5
  Placement = pos=(0,-71,-2.13e-14) rot=(1,0,0;0.785398rad)
  Support = -> [DatumPlane007]
  expr: Constraints[10] = <<sp>>.insertFAVDistBord
  expr: Constraints[12] = <<sp>>.insertFAVDistBord / 2
  expr: Constraints[13] = <<sp>>.largeurModuleBase
  expr: Constraints[14] = <<sp>>.insertFavDistAuZeroDuPLan
  expr: Constraints[15] = <<sp>>.epaisseurParois
  expr: Constraints[16] = <<sp>>.epaisseurParois
  sketch-geometry (6):
    g0: LineSegment StartX=-68.5 StartY=14.7426 StartZ=0 EndX=-72.5 EndY=14.7426 EndZ=0
    g1: LineSegment StartX=-72.5 StartY=14.7426 StartZ=0 EndX=-72.5 EndY=6.74264 EndZ=0
    g2: LineSegment StartX=-72.5 StartY=6.74264 StartZ=0 EndX=-64.5 EndY=6.74264 EndZ=0
    g3: LineSegment StartX=-64.5 StartY=6.74264 StartZ=0 EndX=-64.5 EndY=10.7426 EndZ=0
    g4: ArcOfCircle CenterX=-68.5 CenterY=10.7426 CenterZ=0 NormalX=0 NormalY=0 NormalZ=1 AngleXU=0 Radius=4 StartAngle=-4.5377e-12 EndAngle=1.5708
    g5: GeomPoint X=-75 Y=4.24264 Z=0
  constraints (17):
    c: Horizontal(g0)
    c: Coincident(g0,g1)
    c: Vertical(g1)
    c: Coincident(g1,g2)
    c: Horizontal(g2)
    c: Coincident(g2,g3)
    c: Vertical(g3)
    c: Equal(g3,g0)
    c: Equal(g2,g1)
    c: Coincident(g0,g4)
    c: DistanceX(g2,g2) = 8
    c: Tangent(g4,g3) = -1.5708
    c: DistanceX(g0,g0) = 4
    c: DistanceX(g5,g-1) = 75
    c: DistanceY(g-1,g5) = 4.24264
    c: DistanceY(g5,g1) = 2.5
    c: DistanceX(g5,g1) = 2.5
FEATURE [PartDesign::Pad] Pad006  label="padInsertFavGauch"
  AllowMultiFace = false
  BaseFeature = -> Pad005
  Direction = (0,-0.707107,0.707107)
  Length = 10
  Length2 = 100
  Profile = -> Sketch017
  Type = 2
FEATURE [Sketcher::SketchObject] Sketch018  label="skPercageInsertFavDroit"
  FullyConstrained = true
  MapMode = 5
  Placement = pos=(0,-71,-2.13e-14) rot=(1,0,0;0.785398rad)
  Support = -> [DatumPlane007]
  expr: Constraints[0] = <<sp>>.insertDiamPercage
  expr: Constraints[1] = <<sp>>.insertFavDistAuZeroDuPLan + <<sp>>.epaisseurParois + <<sp>>.insertFAVDistBord / 2
  expr: Constraints[2] = <<sp>>.epaisseurParois + <<sp>>.insertFAVDistBord / 2
  expr: Constraints[7] = <<sp>>.largeurModuleBase - 2 * <<sp>>.epaisseurParois - <<sp>>.insertFAVDistBord
  sketch-geometry (3):
    g0: Circle CenterX=-6.5 CenterY=10.7426 CenterZ=0 NormalX=0 NormalY=0 NormalZ=1 AngleXU=0 Radius=2
    g1: Circle CenterX=-68.5 CenterY=10.7426 CenterZ=0 NormalX=0 NormalY=0 NormalZ=1 AngleXU=0 Radius=2
    g2: LineSegment StartX=-68.5 StartY=10.7426 StartZ=0 EndX=-6.5 EndY=10.7426 EndZ=0
  constraints (8):
    c: Diameter(g0) = 4
    c: DistanceY(g-1,g0) = 10.7426
    c: DistanceX(g0,g-1) = 6.5
    c: Equal(g0,g1)
    c: Coincident(g2,g1)
    c: Coincident(g2,g0)
    c: Horizontal(g2)
    c: DistanceX(g2,g2) = 62
FEATURE [PartDesign::Pocket] Pocket010  label="trouInsertFavDroit"
  AllowMultiFace = false
  BaseFeature = -> Pad006
  Direction = (0,0.707107,-0.707107)
  Length = 8
  Length2 = 100
  Profile = -> Sketch018
  Reversed = true
  Type = 0
  expr: Length = <<sp>>.insertFavProfondeur
FEATURE [PartDesign::Body] Body001  label="base"
  BaseFeature = -> Slice_child0
  Group = -> [Clone,Thickness,DatumPlane001,Sketch002,Pad001,Sketch003,Pocket,DatumPlane002,Sketch004,Pocket001,Sketch005,Pocket002,Sketch006,Pocket003,DatumPlane003,DatumPlane004,Sketch008,Pad003,Sketch009,Pad004,Sketch010,Pocket004,Sketch011,Pocket005,DatumPlane005,Sketch012,Pocket006,Sketch014,Pocket008,LinearPattern,LinearPattern001,DatumPlane006,Sketch015,Pocket009,LinearPattern002,LinearPattern003,+3 more]
  Origin = -> Origin002
  Tip = -> Pocket015
FEATURE [PartDesign::Plane] DatumPlane011  label="planFaceAvant"
  AttachmentOffset = pos=(0,0,93.2843) rot=(-1,0,0;0.785398rad)
  Length = 123.775
  MapMode = 5
  Placement = pos=(0,-93.2843,-2.07e-14) rot=(1,0,0;0.785398rad)
  ResizeMode = 0
  Support = -> [XZ_Plane003]
  Width = 165.093
  expr: .AttachmentOffset.Base.z = <<sp>>.planFaceAvant
FEATURE [Sketcher::SketchObject] Sketch030  label="sk_rebordFav"
  FullyConstrained = true
  MapMode = 5
  Placement = pos=(0,-71,-2.13e-14) rot=(1,0,0;0.785398rad)
  Support = -> [DatumPlane007]
  expr: Constraints[0] = <<sp>>.insertFavDistAuZeroDuPLan
  expr: Constraints[19] = <<sp>>.epaisseurParois
  expr: Constraints[20] = <<sp>>.favEpBordure
  expr: Constraints[21] = <<sp>>.favDistBordPlan
  expr: Constraints[22] = <<sp>>.largeurModuleBase - 2 * <<sp>>.epaisseurParois
  expr: Constraints[23] = <<sp>>.favEpBordure
  expr: Constraints[24] = <<sp>>.Face - <<sp>>.epaisseurParois
  expr: Constraints[25] = <<sp>>.favEpBordure
  sketch-geometry (9):
    g0: GeomPoint X=0 Y=4.24264 Z=0
    g1: LineSegment StartX=-72.5 StartY=20.9853 StartZ=0 EndX=-72.5 EndY=81.7426 EndZ=0
    g2: LineSegment StartX=-72.5 StartY=81.7426 StartZ=0 EndX=-2.5 EndY=81.7426 EndZ=0
    g3: LineSegment StartX=-2.5 StartY=81.7426 StartZ=0 EndX=-2.5 EndY=20.9853 EndZ=0
    g4: LineSegment StartX=-2.5 StartY=20.9853 StartZ=0 EndX=-4 EndY=20.9853 EndZ=0
    g5: LineSegment StartX=-4 StartY=20.9853 StartZ=0 EndX=-4 EndY=80.2426 EndZ=0
    g6: LineSegment StartX=-4 StartY=80.2426 StartZ=0 EndX=-71 EndY=80.2426 EndZ=0
    g7: LineSegment StartX=-71 StartY=80.2426 StartZ=0 EndX=-71 EndY=20.9853 EndZ=0
    g8: LineSegment StartX=-71 StartY=20.9853 StartZ=0 EndX=-72.5 EndY=20.9853 EndZ=0
  constraints (26):
    c: DistanceY(g-1,g0) = 4.24264
    c: Vertical(g0,g-1)
    c: Vertical(g1)
    c: Coincident(g1,g2)
    c: Horizontal(g2)
    c: Coincident(g2,g3)
    c: Vertical(g3)
    c: Coincident(g3,g4)
    c: Horizontal(g4)
    c: Coincident(g4,g5)
    c: Vertical(g5)
    c: Coincident(g5,g6)
    c: Horizontal(g6)
    c: Coincident(g6,g7)
    c: Vertical(g7)
    c: Coincident(g7,g8)
    c: Coincident(g8,g1)
    c: Horizontal(g8)
    c: Horizontal(g7,g4)
    c: DistanceX(g3,g0) = 2.5
    c: DistanceX(g4,g4) = 1.5
    c: DistanceY(g0,g3) = 16.7426
    c: DistanceX(g1,g3) = 70
    c: DistanceY(g5,g2) = 1.5
    c: DistanceY(g0,g2) = 77.5
    c: DistanceX(g1,g7) = 1.5
FEATURE [PartDesign::Pad] Pad014  label="favRebordSupport"
  AllowMultiFace = false
  BaseFeature = -> Pocket010
  Direction = (0,-0.707107,0.707107)
  Length = 10
  Length2 = 100
  Profile = -> Sketch030
  Type = 3
  UpToFace = -> Pocket010 [Face13]
FEATURE [PartDesign::Pad] Pad015  label="favRebord"
  AllowMultiFace = false
  BaseFeature = -> Pad014
  Direction = (0,-0.707107,0.707107)
  Length = 4.15
  Length2 = 100
  Profile = -> Sketch030
  Reversed = true
  Type = 0
  expr: Length = <<sp>>.favBordureProf
FEATURE [Sketcher::SketchObject] Sketch031  label="sk_bourlet"
  ExternalGeometry = -> [Pad015]
  FullyConstrained = true
  MapMode = 5
  Placement = pos=(-2.5,0,0) rot=(0.57735,0.57735,0.57735;2.0944rad)
  Support = -> [Pad015]
  expr: Constraints[3] = <<sp>>.bourletMaintientRayon - <<sp>>.bourletRayonJeu
  sketch-geometry (2):
    g0: ArcOfCircle CenterX=-11.184 CenterY=55.7855 CenterZ=0 NormalX=0 NormalY=0 NormalZ=1 AngleXU=0 Radius=1.3 StartAngle=5.49779 EndAngle=8.63938
    g1: LineSegment StartX=-12.1032 StartY=56.7048 StartZ=0 EndX=-10.2647 EndY=54.8663 EndZ=0
  constraints (6):
    c: Coincident(g0,g-3)
    c: PointOnObject(g0,g-3)
    c: PointOnObject(g0,g-3)
    c: Radius(g0) = 1.3
    c: Coincident(g1,g0)
    c: Coincident(g1,g0)
FEATURE [PartDesign::Pad] Pad016  label="bourlet"
  AllowMultiFace = false
  BaseFeature = -> Pad015
  Direction = (1,0,0)
  Length = 10
  Length2 = 100
  Profile = -> Sketch031
  Reversed = true
  Type = 3
  UpToFace = -> Pad015 [Face11]
FEATURE [Sketcher::SketchObject] Sketch039
  FullyConstrained = true
  MapMode = 5
  Placement = pos=(0,-93.2843,-2.84e-14) rot=(1,0,0;0.785398rad)
  Support = -> [DatumPlane011]
  expr: Constraints[15] = <<favTrousSp>>.trousDiam
  expr: Constraints[16] = <<favTrousSp>>.visEcartY
  expr: Constraints[17] = <<favTrousSp>>.visEcartX
  expr: Constraints[19] = <<favTrousSp>>.planAdap
  expr: Constraints[20] = <<favTrousSp>>.posAdapY
  sketch-geometry (9):
    g0: LineSegment StartX=-65.475 StartY=92 StartZ=0 EndX=-9.525 EndY=92 EndZ=0
    g1: LineSegment StartX=-9.525 StartY=92 StartZ=0 EndX=-9.525 EndY=46 EndZ=0
    g2: LineSegment StartX=-9.525 StartY=46 StartZ=0 EndX=-65.475 EndY=46 EndZ=0
    g3: LineSegment StartX=-65.475 StartY=46 StartZ=0 EndX=-65.475 EndY=92 EndZ=0
    g4: Circle CenterX=-65.475 CenterY=92 CenterZ=0 NormalX=0 NormalY=0 NormalZ=1 AngleXU=0 Radius=2
    g5: Circle CenterX=-9.525 CenterY=92 CenterZ=0 NormalX=0 NormalY=0 NormalZ=1 AngleXU=0 Radius=2
    g6: Circle CenterX=-65.475 CenterY=46 CenterZ=0 NormalX=0 NormalY=0 NormalZ=1 AngleXU=0 Radius=2
    g7: Circle CenterX=-9.525 CenterY=46 CenterZ=0 NormalX=0 NormalY=0 NormalZ=1 AngleXU=0 Radius=2
    g8: GeomPoint X=-37.5 Y=46 Z=0
  constraints (21):
    c: Coincident(g0,g1)
    c: Coincident(g1,g2)
    c: Coincident(g2,g3)
    c: Coincident(g3,g0)
    c: Horizontal(g0)
    c: Horizontal(g2)
    c: Vertical(g1)
    c: Vertical(g3)
    c: Coincident(g4,g0)
    c: Coincident(g5,g0)
    c: Coincident(g6,g2)
    c: Coincident(g7,g1)
    c: Equal(g4,g5)
    c: Equal(g5,g7)
    c: Equal(g7,g6)
    c: Diameter(g4) = 4
    c: DistanceY(g7,g5) = 46
    c: DistanceX(g6,g7) = 55.95
    c: Symmetric(g6,g7,g8)
    c: DistanceX(g8,g-1) = 37.5
    c: DistanceY(g-1,g7) = 46
FEATURE [PartDesign::Pocket] Pocket018  label="trouVisAdapt"
  BaseFeature = -> Pad016
  Direction = (0,0.707107,-0.707107)
  Length = 5
  Length2 = 5
  Profile = -> Sketch039
  ReferenceAxis = -> Sketch039 [N_Axis]
  Type = 1
FEATURE [Sketcher::SketchObject] Sketch040
  FullyConstrained = true
  MapMode = 5
  Placement = pos=(0,-93.2843,-2.84e-14) rot=(1,0,0;0.785398rad)
  Support = -> [DatumPlane011]
  expr: Constraints[12] = <<favTrousSp>>.planAdap
  expr: Constraints[8] = <<favTrousSp>>.passCableLarg
  expr: Constraints[9] = <<favTrousSp>>.passCableLong
  sketch-geometry (5):
    g0: LineSegment StartX=-47.5 StartY=68 StartZ=0 EndX=-27.5 EndY=68 EndZ=0
    g1: LineSegment StartX=-27.5 StartY=68 StartZ=0 EndX=-27.5 EndY=41.2 EndZ=0
    g2: LineSegment StartX=-27.5 StartY=41.2 StartZ=0 EndX=-47.5 EndY=41.2 EndZ=0
    g3: LineSegment StartX=-47.5 StartY=41.2 StartZ=0 EndX=-47.5 EndY=68 EndZ=0
    g4: GeomPoint X=-37.5 Y=41.2 Z=0
  constraints (13):
    c: Coincident(g0,g1)
    c: Coincident(g1,g2)
    c: Coincident(g2,g3)
    c: Coincident(g3,g0)
    c: Horizontal(g0)
    c: Horizontal(g2)
    c: Vertical(g1)
    c: Vertical(g3)
    c: DistanceX(g2,g1) = 20
    c: DistanceY(g1,g0) = 26.8
    c: DistanceY(g-1,g1) = 41.2
    c: Symmetric(g2,g1,g4)
    c: DistanceX(g4,g-1) = 37.5
FEATURE [PartDesign::Pocket] Pocket019  label="passageCable"
  BaseFeature = -> Pocket018
  Direction = (0,0.707107,-0.707107)
  Length = 5
  Length2 = 5
  Profile = -> Sketch040
  ReferenceAxis = -> Sketch040 [N_Axis]
  Type = 1
FEATURE [PartDesign::Body] Body002  label="faceAvant"
  BaseFeature = -> Slice_child1
  Group = -> [Clone001,Thickness001,DatumPlane007,Sketch016,Pad005,Sketch017,Pad006,Sketch018,Pocket010,DatumPlane011,Sketch030,Pad014,Pad015,Sketch031,Pad016,Sketch039,Pocket018,Sketch040,Pocket019]
  Origin = -> Origin003
  Tip = -> Pocket019
COMPONENT P7 — geometry summary ("visInsertsAdapt"; no construction recipe available for this part):
  bounding box: 61.5 x 42.0 x 41.9 mm
  tessellated surface: 4,112 triangles
  volume: 368 mm^3 (0% of its bounding box)
  symmetry: mirror-symmetric across its x mid-plane
PROVENANCE & LICENSES
A FreeCAD (.FCStd) document from a public repository crawl; recipes are the document's own serialized feature recipes (and, for linked parts, companion documents' recipes).
License: as declared in the source repository (recorded in the dataset sidecar).
